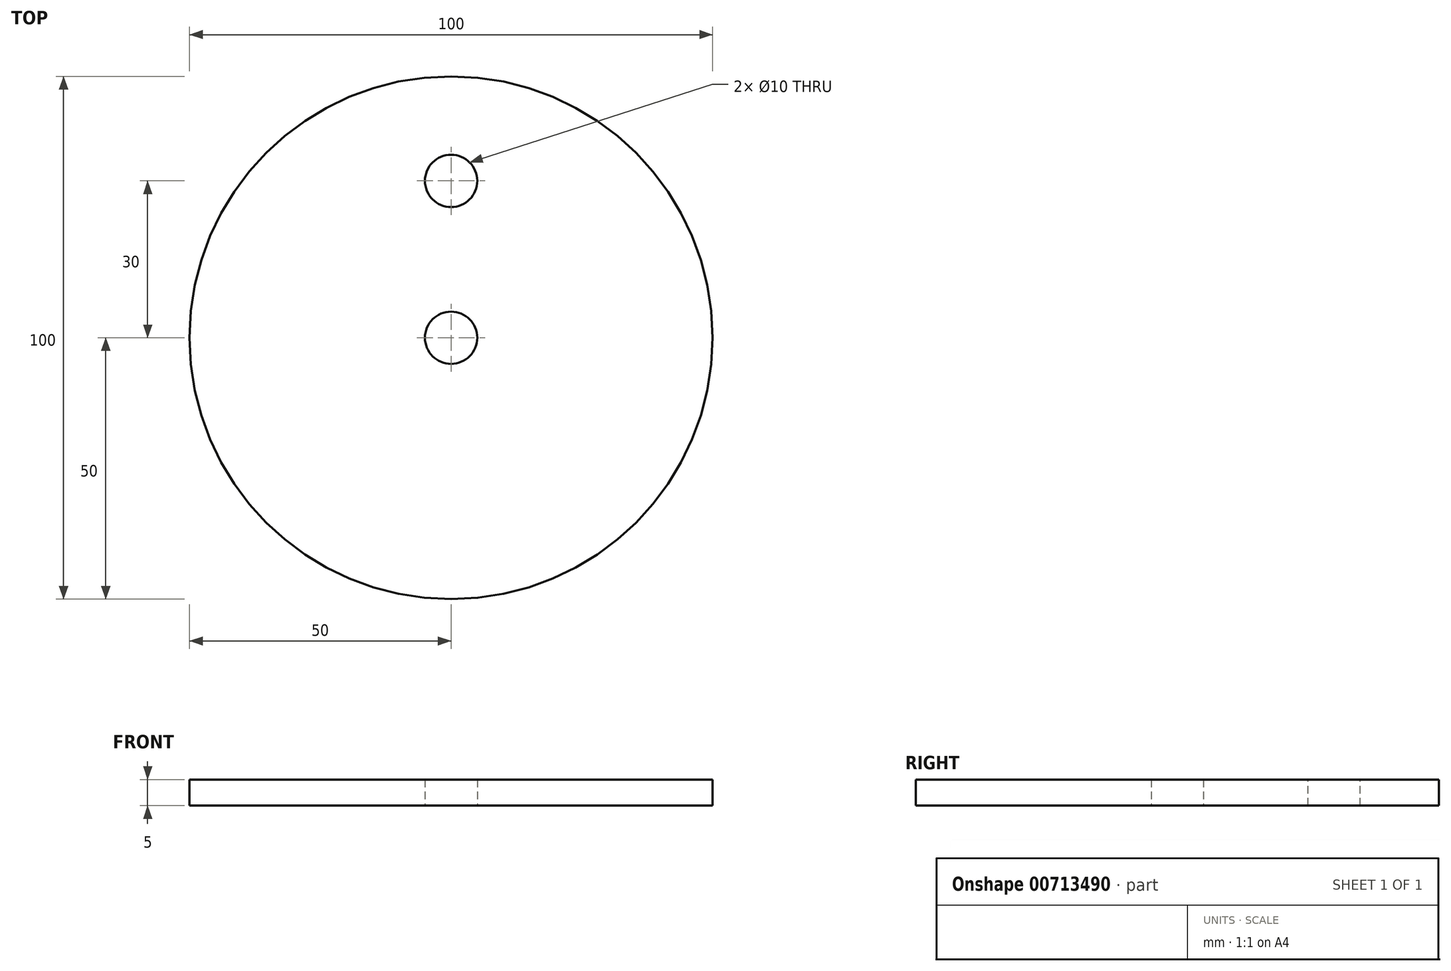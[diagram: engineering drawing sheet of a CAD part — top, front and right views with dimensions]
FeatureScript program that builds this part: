
annotation { "Feature Type Name" : "Feature", "Feature Type Description" : "" }
export const myFeature = defineFeature(function(context is Context, id is Id, definition is map)
    precondition{}
    {
        {
            var Q0;
            Q0=qCreatedBy(makeId("Top.planeOp"),FACE);
            var sketch = newSketch(context, id + "F0", { "sketchPlane" : qUnion([Q0])});
            skCircle(sketch, "E0", {"center": v(0, 0) * mm, "radius": 5 * mm});
            skCircle(sketch, "E1", {"center": v(0, 0) * mm, "radius": 50 * mm});
            skSolve(sketch);
        }
        {
            var Q0;
            Q0=makeQuery(id+"F0.imprint","IMPRINT",FACE,{"disambiguationData":[TD([[makeQuery(id+"F0.imprint","IMPRINT",EDGE,{"derivedFrom":sQuery(id+"F0.wireOp",EDGE,"E0")}),-1.0]])]});
            extrude(context, id + "F1", {"entities" : qUnion([Q0]), "depth" : 5 * mm, "offsetDistance" : 25 * mm});
        }
        {
            var Q0;
            Q0=makeQuery(id+"F1.opExtrude","CAP_FACE",FACE,{"disambiguationData":[OSD([sQuery(id+"F0.wireOp",EDGE,"E0"),sQuery(id+"F0.wireOp",EDGE,"E1")])],"isStart":false});
            var sketch = newSketch(context, id + "F2", { "sketchPlane" : qUnion([Q0])});
            skCircle(sketch, "E2", {"center": v(0, 30) * mm, "radius": 5 * mm});
            skLineSegment(sketch, "E3", {"start": v(0, 30) * mm, "end": v(0, 0) * mm, "construction": true});
            skSolve(sketch);
        }
        {
            var Q0;
            Q0=qSketchRegion(id+"F2",true);
            extrude(context, id + "F3", {"entities" : qUnion([Q0]), "operationType" : NewBodyOperationType.REMOVE, "oppositeDirection" : true, "depth" : 25 * mm, "offsetDistance" : 25 * mm});
        }
    });
